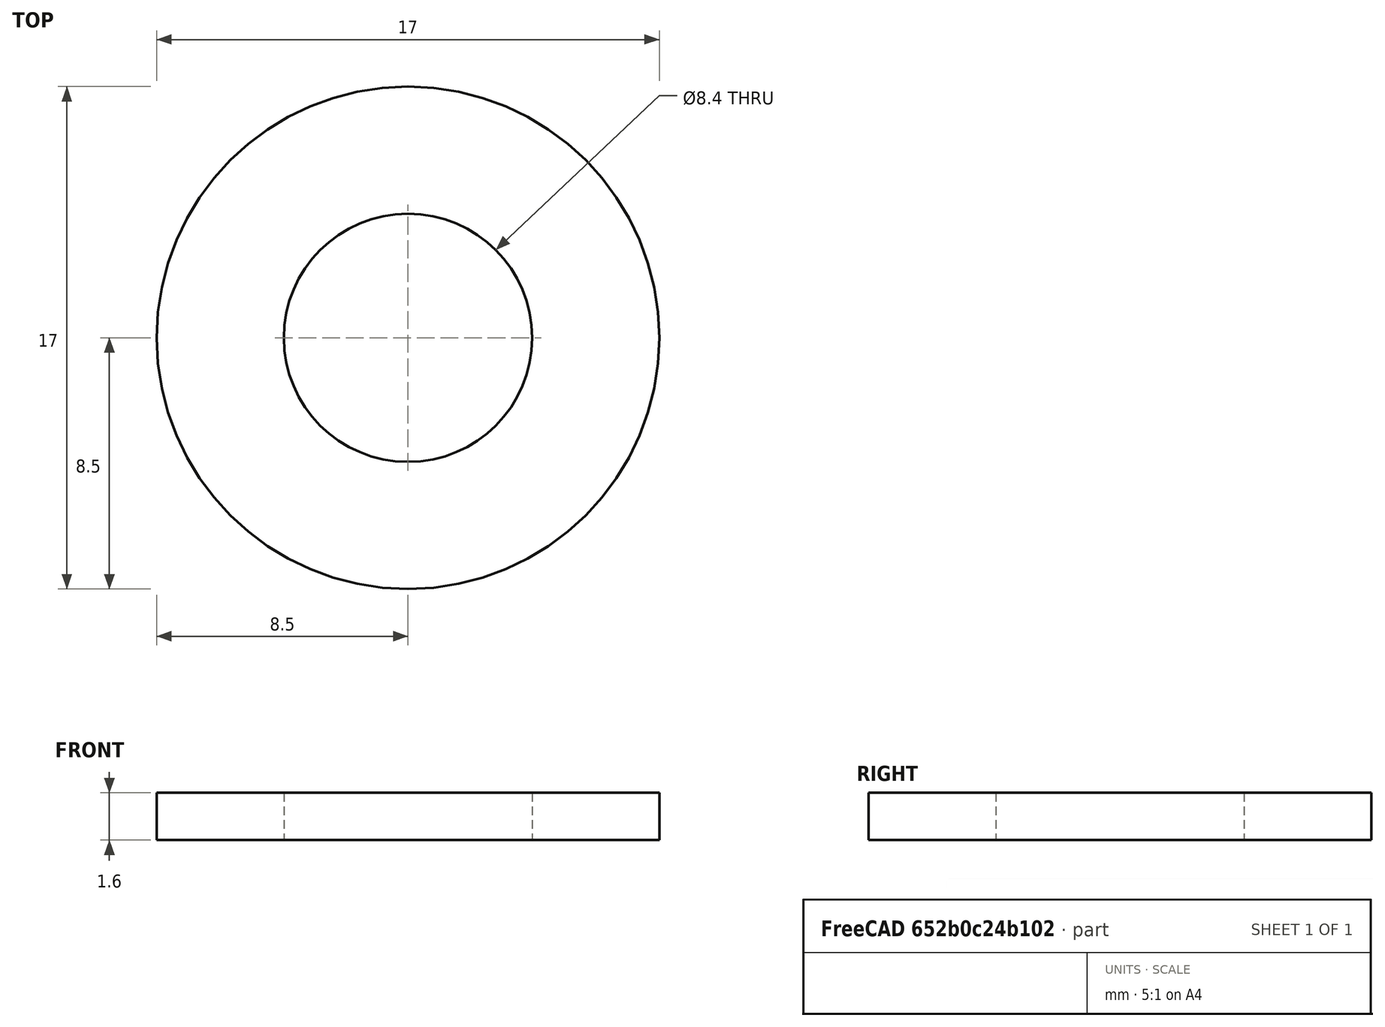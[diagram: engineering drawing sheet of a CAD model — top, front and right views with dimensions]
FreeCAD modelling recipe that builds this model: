
FCSTD DOCUMENT  (FreeCAD 0.14R3700 (Git))
Label: Scheibe DIN 125 - A 8,4
License: CC-BY 3.0
LicenseURL: http://creativecommons.org/licenses/by/3.0/
objects: Sketcher::SketchObject×1, PartDesign::Revolution×1, Part::Feature×1
note: 4 computed .brp shape members not serialized (recipe doc carries the construction recipe); baked Part::Feature solids carry a one-line shape summary decoded from their .brp

FEATURE [Sketcher::SketchObject] Sketch
  Placement = pos=(0,0,0) rot=(0.57735,0.57735,0.57735;2.0944rad)
  sketch-geometry (4):
    g0: LineSegment StartX=4.2 StartY=0 StartZ=0 EndX=8.5 EndY=0 EndZ=0
    g1: LineSegment StartX=8.5 StartY=0 StartZ=0 EndX=8.5 EndY=1.6 EndZ=0
    g2: LineSegment StartX=8.5 StartY=1.6 StartZ=0 EndX=4.2 EndY=1.6 EndZ=0
    g3: LineSegment StartX=4.2 StartY=1.6 StartZ=0 EndX=4.2 EndY=0 EndZ=0
  constraints (12):
    c: Coincident(g0,g1)
    c: Coincident(g1,g2)
    c: Coincident(g2,g3)
    c: Coincident(g3,g0)
    c: Horizontal(g0)
    c: Horizontal(g2)
    c: Vertical(g1)
    c: Vertical(g3)
    c: PointOnObject(g0,g-1)
    c: DistanceY(g1) = 1.6
    c: DistanceX(g-1,g2) = 4.2
    c: DistanceX(g-1,g1) = 8.5
FEATURE [PartDesign::Revolution] Revolution  label="Scheibe DIN 125 - A 8,4 #"
  Angle = 360
  Axis = (0,0,1)
  Base = (0,0,0)
  Placement = pos=(0,0,0) rot=(0.57735,0.57735,0.57735;2.0944rad)
  ReferenceAxis = -> Sketch [V_Axis]
  Reversed = true
  Sketch = -> Sketch
FEATURE [Part::Feature] Revolution001  label="Scheibe DIN 125 - A 8,4 #001"
  Placement = pos=(0,0,0) rot=(0.57735,0.57735,0.57735;2.0944rad)
  shape: bbox 17 x 17 x 1.6 mm, 4 faces (baked)
